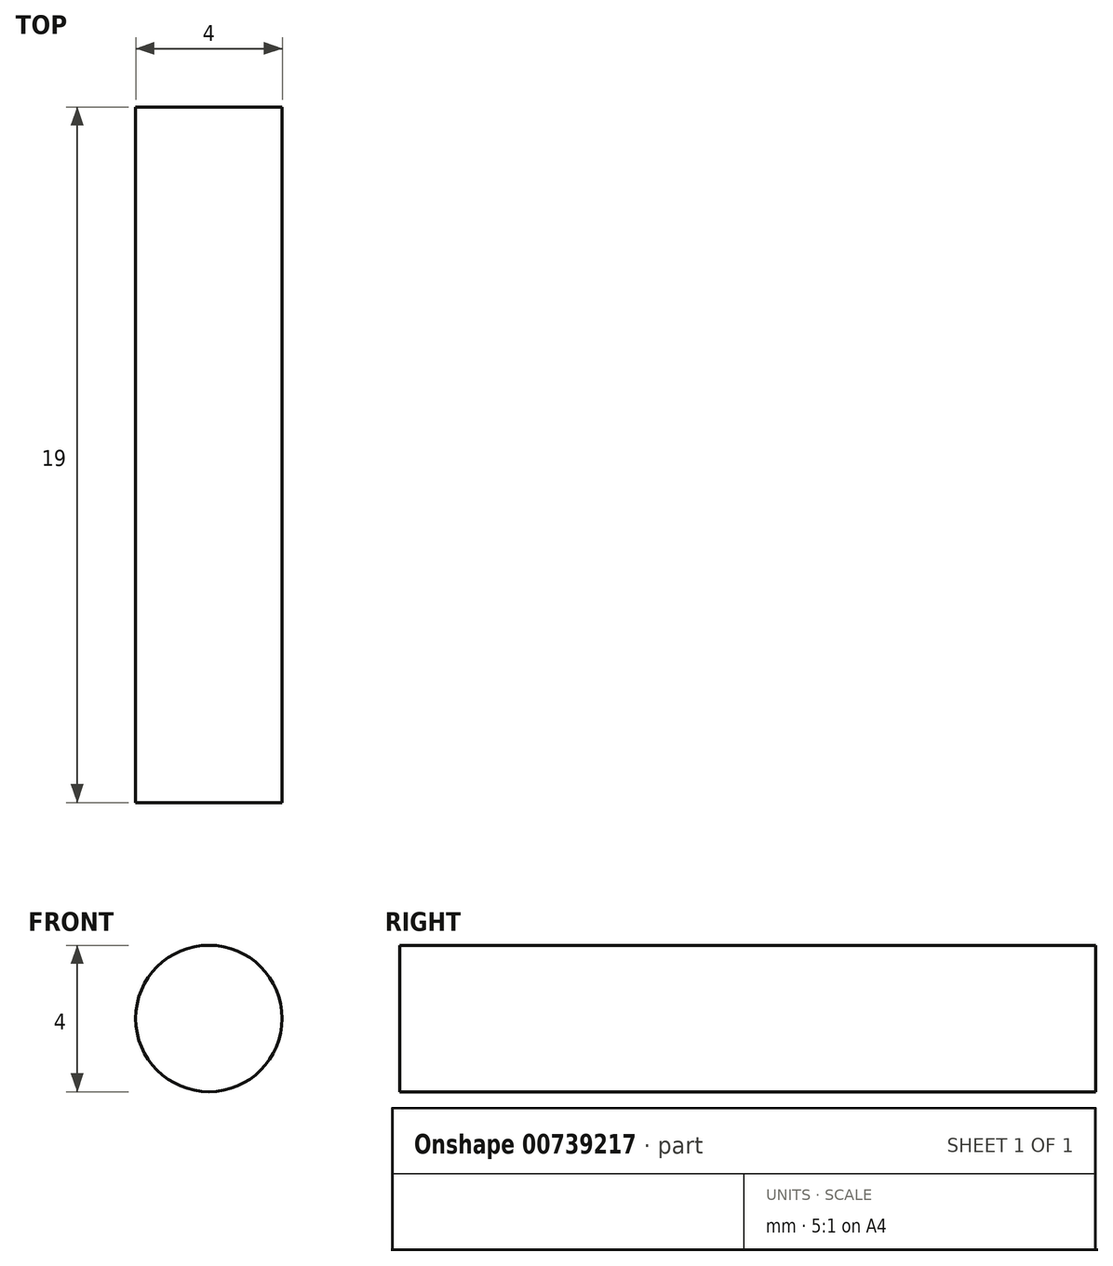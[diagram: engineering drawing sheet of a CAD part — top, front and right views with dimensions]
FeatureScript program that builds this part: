
annotation { "Feature Type Name" : "Feature", "Feature Type Description" : "" }
export const myFeature = defineFeature(function(context is Context, id is Id, definition is map)
    precondition{}
    {
        {
            var Q0;
            Q0=qCreatedBy(makeId("Front.planeOp"),FACE);
            var sketch = newSketch(context, id + "F0", { "sketchPlane" : qUnion([Q0])});
            skCircle(sketch, "E0", {"center": v(0.98, 6.7) * mm, "radius": 2 * mm});
            skSolve(sketch);
        }
        {
            var Q0;
            Q0 = qSketchRegion(id + "F0", true);
            extrude(context, id + "F1", {"entities" : qUnion([Q0]), "depth" : 19 * mm, "offsetDistance" : 25.4 * mm});
        }
    });
